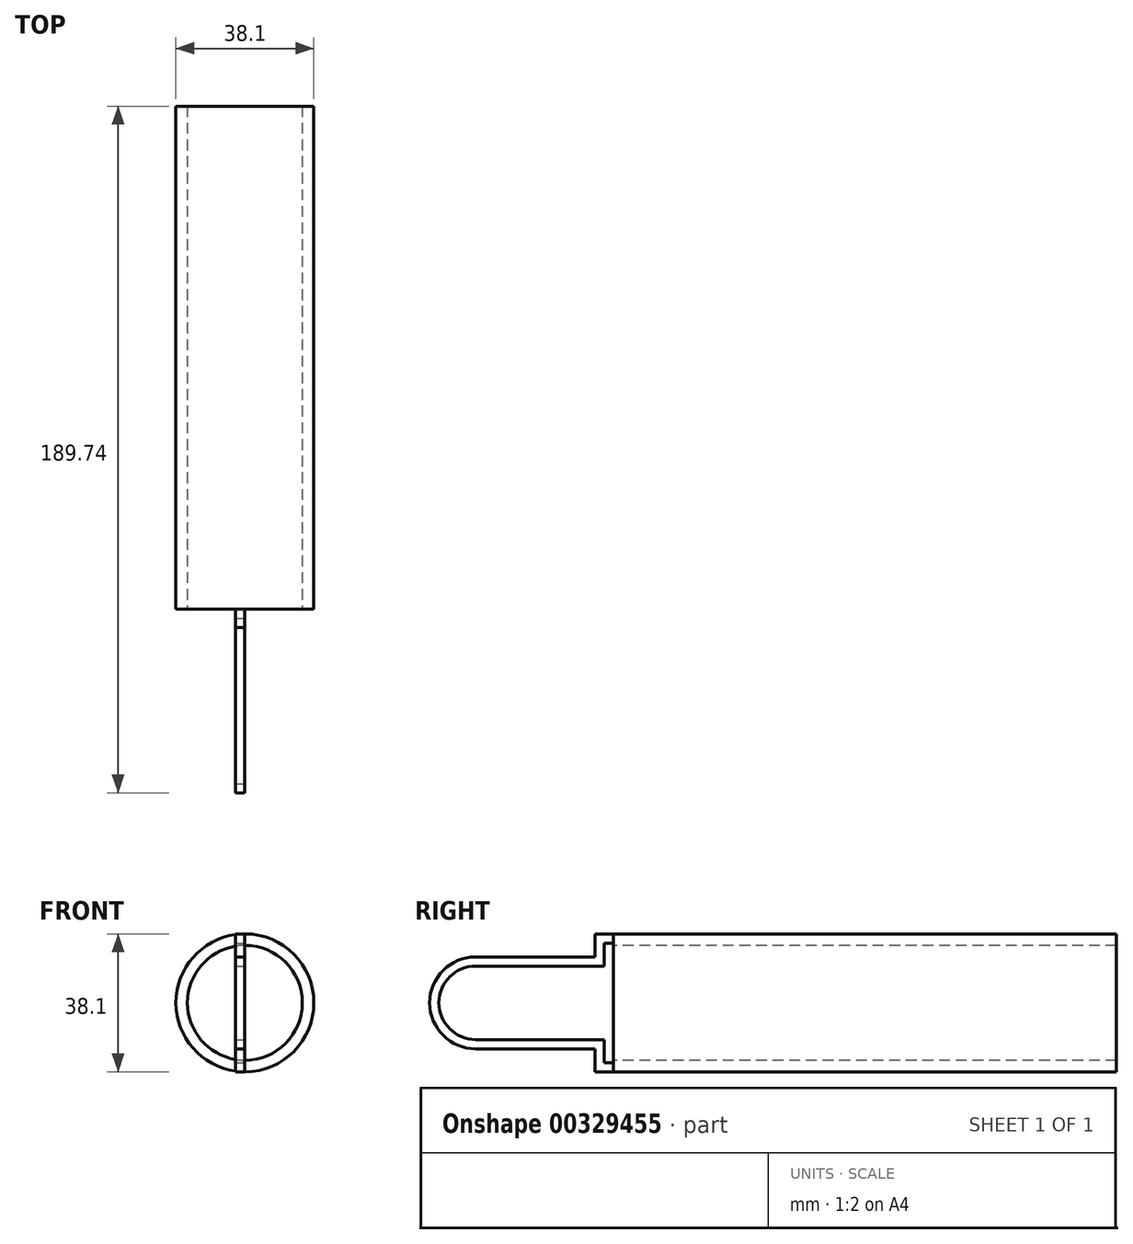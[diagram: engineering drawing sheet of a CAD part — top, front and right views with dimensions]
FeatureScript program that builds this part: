
annotation { "Feature Type Name" : "Feature", "Feature Type Description" : "" }
export const myFeature = defineFeature(function(context is Context, id is Id, definition is map)
    precondition{}
    {
        {
            var Q0;
            Q0=qCreatedBy(makeId("Front.planeOp"),FACE);
            var sketch = newSketch(context, id + "F0", { "sketchPlane" : qUnion([Q0])});
            skCircle(sketch, "E0", {"center": v(0, 0) * mm, "radius": 19.05 * mm});
            skCircle(sketch, "E1", {"center": v(0, 0) * mm, "radius": 15.88 * mm});
            skSolve(sketch);
        }
        {
            var Q0;
            Q0 = qSketchRegion(id + "F0", true);
            extrude(context, id + "F1", {"entities" : qUnion([Q0]), "oppositeDirection" : true, "depth" : 138.94 * mm});
        }
        {
            var Q0;
            Q0=qCreatedBy(makeId("Right.planeOp"),FACE);
            var sketch = newSketch(context, id + "F2", { "sketchPlane" : qUnion([Q0])});
            skLineSegment(sketch, "E2.bottom", {"start": v(0, 12.7) * mm, "end": v(-2.54, 12.7) * mm});
            skLineSegment(sketch, "E2.top", {"start": v(0, -12.7) * mm, "end": v(-2.54, -12.7) * mm});
            skLineSegment(sketch, "E2.left", {"start": v(0, 12.7) * mm, "end": v(0, 10.16) * mm});
            skLineSegment(sketch, "E2.right", {"start": v(-50.8, 0) * mm, "end": v(-50.8, 0) * mm});
            skPoint(sketch, "E3.visualSharp", {"position": v(-50.8, 12.7) * mm});
            skArc(sketch, "E3.filletArc", {"start": v(-38.1, 12.7) * mm, "mid": v(-47.08, 8.98) * mm, "end": v(-50.8, 0) * mm});
            skPoint(sketch, "E4.visualSharp", {"position": v(-50.8, -12.7) * mm});
            skArc(sketch, "E4.filletArc", {"start": v(-50.8, 0) * mm, "mid": v(-47.08, -8.98) * mm, "end": v(-38.1, -12.7) * mm});
            skLineSegment(sketch, "E5.0", {"start": v(0, -10.16) * mm, "end": v(-38.1, -10.16) * mm});
            skArc(sketch, "E5.1", {"start": v(-48.26, 0) * mm, "mid": v(-45.28, -7.18) * mm, "end": v(-38.1, -10.16) * mm});
            skArc(sketch, "E5.2", {"start": v(-38.1, 10.16) * mm, "mid": v(-45.28, 7.18) * mm, "end": v(-48.26, 0) * mm});
            skLineSegment(sketch, "E5.3", {"start": v(0, 10.16) * mm, "end": v(-38.1, 10.16) * mm});
            skLineSegment(sketch, "E6.trimOffspring", {"start": v(0, -10.16) * mm, "end": v(0, -12.7) * mm});
            skLineSegment(sketch, "E7.top", {"start": v(-5.08, 19.05) * mm, "end": v(-2.54, 19.05) * mm});
            skLineSegment(sketch, "E7.left", {"start": v(-5.08, 12.7) * mm, "end": v(-5.08, 19.05) * mm});
            skLineSegment(sketch, "E7.right", {"start": v(-2.54, 12.7) * mm, "end": v(-2.54, 16.51) * mm});
            skLineSegment(sketch, "E8.bottom", {"start": v(-2.54, 19.05) * mm, "end": v(0, 19.05) * mm});
            skLineSegment(sketch, "E8.top", {"start": v(-2.54, 16.51) * mm, "end": v(0, 16.51) * mm});
            skLineSegment(sketch, "E8.right", {"start": v(0, 19.05) * mm, "end": v(0, 16.51) * mm});
            skLineSegment(sketch, "E9.top", {"start": v(-5.08, -19.05) * mm, "end": v(-2.54, -19.05) * mm});
            skLineSegment(sketch, "E9.left", {"start": v(-5.08, -12.7) * mm, "end": v(-5.08, -19.05) * mm});
            skLineSegment(sketch, "E9.right", {"start": v(-2.54, -12.7) * mm, "end": v(-2.54, -16.5) * mm});
            skLineSegment(sketch, "E10.bottom", {"start": v(-2.54, -19.05) * mm, "end": v(0, -19.05) * mm});
            skLineSegment(sketch, "E10.top", {"start": v(-2.54, -16.5) * mm, "end": v(0, -16.5) * mm});
            skLineSegment(sketch, "E10.right", {"start": v(0, -19.05) * mm, "end": v(0, -16.5) * mm});
            skLineSegment(sketch, "E11.trimOffspring", {"start": v(-5.08, 12.7) * mm, "end": v(-38.1, 12.7) * mm});
            skLineSegment(sketch, "E12.trimOffspring", {"start": v(-5.08, -12.7) * mm, "end": v(-38.1, -12.7) * mm});
            skSolve(sketch);
        }
        {
            var Q0;
            Q0=makeQuery(id+"F2.imprint","IMPRINT",FACE,{"disambiguationData":[TD([[makeQuery(id+"F2.imprint","IMPRINT",EDGE,{"derivedFrom":sQuery(id+"F2.wireOp",EDGE,"E2.bottom")}),1.0]])]});
            extrude(context, id + "F3", {"entities" : qUnion([Q0]), "oppositeDirection" : true, "depth" : 2.54 * mm});
        }
        {
            var Q0;
            Q0=makeQuery(id+"F3.opExtrude","CAP_FACE",FACE,{"disambiguationData":[OSD([sQuery(id+"F2.wireOp",EDGE,"E2.bottom"),sQuery(id+"F2.wireOp",EDGE,"E2.top"),sQuery(id+"F2.wireOp",EDGE,"E2.left"),sQuery(id+"F2.wireOp",EDGE,"E3.filletArc"),sQuery(id+"F2.wireOp",EDGE,"E4.filletArc"),sQuery(id+"F2.wireOp",EDGE,"E5.0"),sQuery(id+"F2.wireOp",EDGE,"E5.1"),sQuery(id+"F2.wireOp",EDGE,"E5.2"),sQuery(id+"F2.wireOp",EDGE,"E5.3"),sQuery(id+"F2.wireOp",EDGE,"E6.trimOffspring"),sQuery(id+"F2.wireOp",EDGE,"E7.top"),sQuery(id+"F2.wireOp",EDGE,"E7.left"),sQuery(id+"F2.wireOp",EDGE,"E7.right"),sQuery(id+"F2.wireOp",EDGE,"E8.bottom"),sQuery(id+"F2.wireOp",EDGE,"E8.top"),sQuery(id+"F2.wireOp",EDGE,"E8.right"),sQuery(id+"F2.wireOp",EDGE,"E9.top"),sQuery(id+"F2.wireOp",EDGE,"E9.left"),sQuery(id+"F2.wireOp",EDGE,"E9.right"),sQuery(id+"F2.wireOp",EDGE,"E10.bottom"),sQuery(id+"F2.wireOp",EDGE,"E10.top"),sQuery(id+"F2.wireOp",EDGE,"E10.right"),sQuery(id+"F2.wireOp",EDGE,"E11.trimOffspring"),sQuery(id+"F2.wireOp",EDGE,"E12.trimOffspring")])],"isStart":true});
            var sketch = newSketch(context, id + "F4", { "sketchPlane" : qUnion([Q0])});
            skLineSegment(sketch, "E13.bottom", {"start": v(0, 10.16) * mm, "end": v(-2.54, 10.16) * mm});
            skLineSegment(sketch, "E13.top", {"start": v(0, 12.7) * mm, "end": v(-2.54, 12.7) * mm});
            skLineSegment(sketch, "E13.left", {"start": v(0, 10.16) * mm, "end": v(0, 12.7) * mm});
            skLineSegment(sketch, "E13.right", {"start": v(-2.54, 10.16) * mm, "end": v(-2.54, 12.7) * mm});
            skLineSegment(sketch, "E14.bottom", {"start": v(0, -10.16) * mm, "end": v(-2.54, -10.16) * mm});
            skLineSegment(sketch, "E14.top", {"start": v(0, -12.7) * mm, "end": v(-2.54, -12.7) * mm});
            skLineSegment(sketch, "E14.left", {"start": v(0, -10.16) * mm, "end": v(0, -12.7) * mm});
            skLineSegment(sketch, "E14.right", {"start": v(-2.54, -10.16) * mm, "end": v(-2.54, -12.7) * mm});
            skSolve(sketch);
        }
        {
            var Q0;
            Q0 = qSketchRegion(id + "F4", true);
            extrude(context, id + "F5", {"entities" : qUnion([Q0]), "operationType" : NewBodyOperationType.REMOVE, "oppositeDirection" : true, "depth" : 25.4 * mm});
        }
    });
